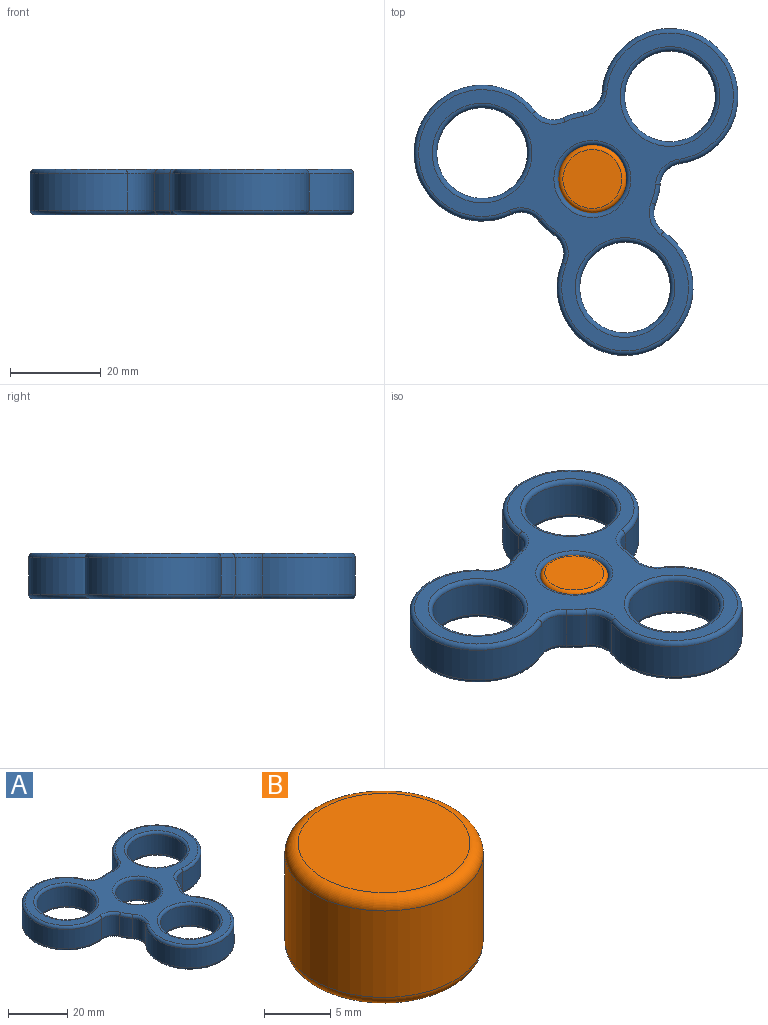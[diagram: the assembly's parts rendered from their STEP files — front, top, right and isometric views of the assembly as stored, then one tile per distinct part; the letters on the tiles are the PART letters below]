
ASSEMBLY  parts=2 mates=1
PART A: 50 faces, bbox 75.8x70x10 mm
  f0: cylinder r=15mm len=8mm, axis (0,0,-1), area 36.4mm2, adj f12,f14,f19,f32
  f1: cylinder r=15mm len=30mm, axis (0,0,-1), area 539mm2, adj f12,f13,f23,f36
  f2: cylinder r=15mm len=8mm, axis (0,0,-1), area 36.4mm2, adj f13,f17,f27,f40
  f3: cylinder r=15mm len=30mm, axis (0,0,-1), area 539mm2, adj f16,f17,f28,f39
  f4: cylinder r=15mm len=8mm, axis (0,0,-1), area 36.4mm2, adj f15,f16,f24,f35
  f5: cylinder r=10mm len=20mm, axis (0,0,-1), area 502.7mm2, adj f43,f49
  f6: cylinder r=10mm len=20mm, axis (0,0,-1), area 502.7mm2, adj f42,f48
  f7: cylinder r=15mm len=30mm, axis (0,0,-1), area 539mm2, adj f14,f15,f20,f31
  f8: cylinder r=10mm len=20mm, axis (0,0,-1), area 502.7mm2, adj f45,f46
  f9: cylinder r=7.5mm len=15mm, axis (0,0,-1), area 377mm2, adj f44,f47
  f10: plane 71.3x65.5mm, normal (0,0,1), area 1067.4mm2, adj f18,f19,f20,f21,f22,f23,f24,f25
  f11: plane 71.3x65.5mm, normal (0,0,-1), area 1067.4mm2, adj f30,f31,f32,f33,f34,f35,f36,f37
  f12: cylinder r=5mm len=8mm, axis (0,0,1), area 54mm2, adj f0,f1,f21,f34
  f13: cylinder r=5mm len=8mm, axis (0,0,1), area 54mm2, adj f1,f2,f25,f38
  f14: cylinder r=5mm len=8mm, axis (0,0,1), area 54mm2, adj f0,f7,f18,f30
  f15: cylinder r=5mm len=8mm, axis (0,0,1), area 54mm2, adj f4,f7,f22,f33
  f16: cylinder r=5mm len=8mm, axis (0,0,1), area 54mm2, adj f3,f4,f26,f37
  f17: cylinder r=5mm len=8mm, axis (0,0,1), area 54mm2, adj f2,f3,f29,f41
  f18: torus R=6mm, axis (0,0,1), area 11.4mm2, adj f10,f14,f19,f20
  f19: torus R=14mm, axis (0,0,1), area 7mm2, adj f0,f10,f18,f21
  f20: torus R=14mm, axis (0,0,1), area 103.3mm2, adj f7,f10,f18,f22
  f21: torus R=6mm, axis (0,0,1), area 11.4mm2, adj f10,f12,f19,f23
  f22: torus R=6mm, axis (0,0,1), area 11.4mm2, adj f10,f15,f20,f24
  f23: torus R=14mm, axis (0,0,1), area 103.3mm2, adj f1,f10,f21,f25
  f24: torus R=14mm, axis (0,0,1), area 7mm2, adj f4,f10,f22,f26
  f25: torus R=6mm, axis (0,0,1), area 11.4mm2, adj f10,f13,f23,f27
  f26: torus R=6mm, axis (0,0,1), area 11.4mm2, adj f10,f16,f24,f28
  f27: torus R=14mm, axis (0,0,1), area 7mm2, adj f2,f10,f25,f29
  f28: torus R=14mm, axis (0,0,1), area 103.3mm2, adj f3,f10,f26,f29
  f29: torus R=6mm, axis (0,0,1), area 11.4mm2, adj f10,f17,f27,f28
  f30: torus R=6mm, axis (0,0,1), area 11.4mm2, adj f11,f14,f31,f32
  f31: torus R=14mm, axis (0,0,1), area 103.3mm2, adj f7,f11,f30,f33
  f32: torus R=14mm, axis (0,0,1), area 7mm2, adj f0,f11,f30,f34
  f33: torus R=6mm, axis (0,0,1), area 11.4mm2, adj f11,f15,f31,f35
  f34: torus R=6mm, axis (0,0,1), area 11.4mm2, adj f11,f12,f32,f36
  f35: torus R=14mm, axis (0,0,1), area 7mm2, adj f4,f11,f33,f37
  f36: torus R=14mm, axis (0,0,1), area 103.3mm2, adj f1,f11,f34,f38
  f37: torus R=6mm, axis (0,0,1), area 11.4mm2, adj f11,f16,f35,f39
  f38: torus R=6mm, axis (0,0,1), area 11.4mm2, adj f11,f13,f36,f40
  f39: torus R=14mm, axis (0,0,1), area 103.3mm2, adj f3,f11,f37,f41
  f40: torus R=14mm, axis (0,0,1), area 7mm2, adj f2,f11,f38,f41
  f41: torus R=6mm, axis (0,0,1), area 11.4mm2, adj f11,f17,f39,f40
  f42: torus R=11mm, axis (0,0,1), area 102.3mm2, adj f6,f11
  f43: torus R=11mm, axis (0,0,1), area 102.3mm2, adj f5,f11
  f44: torus R=8.5mm, axis (0,0,1), area 77.6mm2, adj f9,f11
  f45: torus R=11mm, axis (0,0,1), area 102.3mm2, adj f8,f11
  f46: torus R=11mm, axis (0,0,1), area 102.3mm2, adj f8,f10
  f47: torus R=8.5mm, axis (0,0,1), area 77.6mm2, adj f9,f10
  f48: torus R=11mm, axis (0,0,1), area 102.3mm2, adj f6,f10
  f49: torus R=11mm, axis (0,0,1), area 102.3mm2, adj f5,f10
PART B: 5 faces, bbox 16.2x16.2x10 mm
  f0: cylinder r=7.5mm len=15mm, axis (0,0,-1), area 377mm2, adj f3,f4
  f1: plane 13x13mm, normal (0,0,1), area 132.7mm2, adj f4
  f2: plane 13x13mm, normal (0,0,-1), area 132.7mm2, adj f3
  f3: torus R=6.5mm, axis (0,0,1), area 70.4mm2, adj f0,f2
  f4: torus R=6.5mm, axis (0,0,1), area 70.4mm2, adj f0,f1
PLACE A rot(axis=(0,0,-1),103.2deg) t=(-4.96,6.33,-0.59)mm
PLACE B t=(-4.96,6.33,4.41)mm fixed
MATE revolute B.f0 <-> A.f9  axis (0,0,-1) through (-4.96,6.33,4.41)mm
